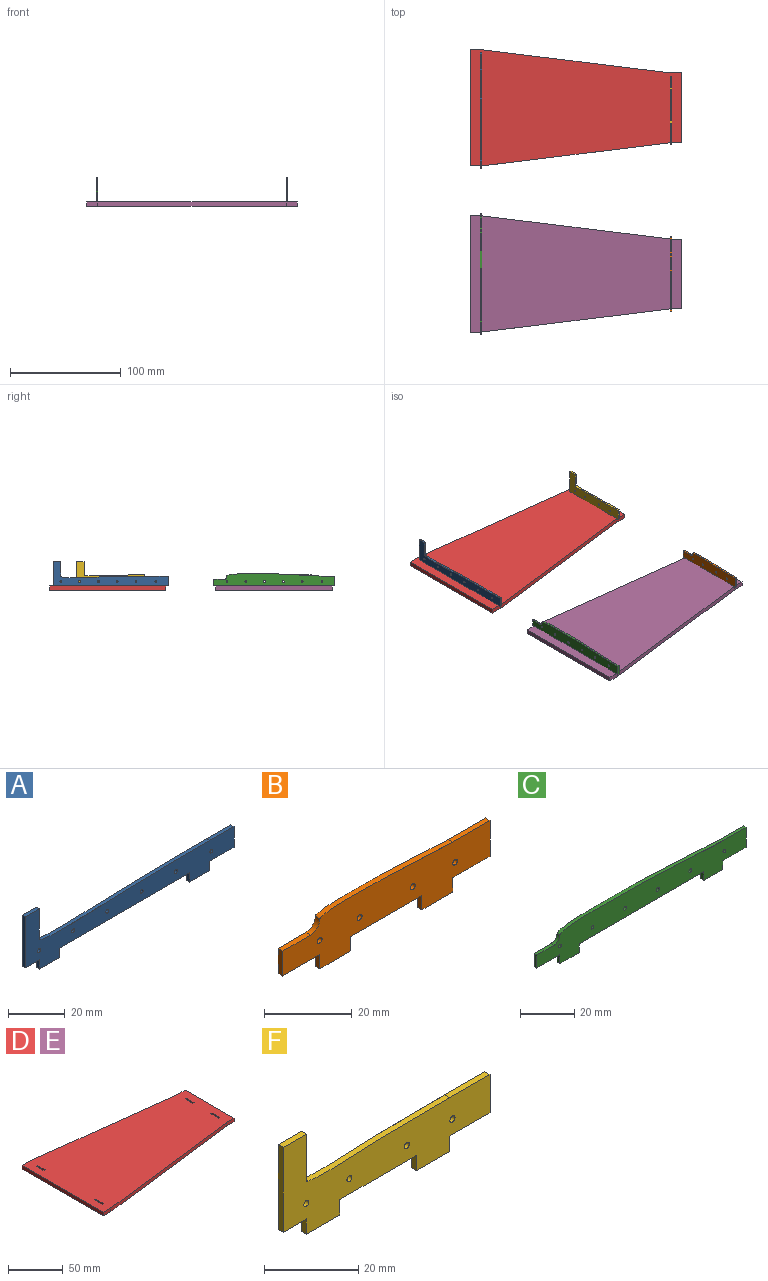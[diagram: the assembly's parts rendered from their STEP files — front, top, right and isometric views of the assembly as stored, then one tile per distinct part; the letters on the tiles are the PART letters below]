
ASSEMBLY  parts=6 mates=13
PART A: 23 faces, bbox 104x1.5x26 mm
  f0: plane 4x1.5mm, normal (1,0,0), area 6mm2, adj f1,f20,f21,f22
  f1: plane 12x1.5mm, normal (0,0,-1), area 18mm2, adj f0,f2,f21,f22
  f2: plane 8.89x1.5mm, normal (1,0,0), area 13.3mm2, adj f1,f3,f21,f22
  f3: plane 12x1.5mm, normal (0,0,1), area 18mm2, adj f2,f4,f21,f22
  f4: extruded ~85x1.61mm, area 127.8mm2, adj f3,f5,f21,f22
  f5: plane 13.08x1.5mm, normal (1,0,0), area 19.6mm2, adj f4,f6,f21,f22
  f6: plane 7x1.5mm, normal (0,0,1), area 10.5mm2, adj f5,f7,f21,f22
  f7: plane 22x1.5mm, normal (-1,0,0), area 33mm2, adj f6,f8,f21,f22
  f8: plane 7x1.5mm, normal (0,0,-1), area 10.5mm2, adj f7,f9,f21,f22
  f9: plane 4x1.5mm, normal (-1,0,0), area 6mm2, adj f8,f10,f21,f22
  f10: plane 10x1.5mm, normal (0,0,-1), area 15mm2, adj f9,f11,f21,f22
  f11: plane 4x1.5mm, normal (1,0,0), area 6mm2, adj f10,f12,f21,f22
  f12: plane 65x1.5mm, normal (0,0,-1), area 97.5mm2, adj f11,f13,f21,f22
  f13: plane 4x1.5mm, normal (-1,0,0), area 6mm2, adj f12,f20,f21,f22
  f14: cylinder r=0.76mm len=1.52mm, axis (0,1,0), area 7.2mm2, adj f21,f22
  f15: cylinder r=0.76mm len=1.52mm, axis (0,1,0), area 7.2mm2, adj f21,f22
  f16: cylinder r=0.76mm len=1.52mm, axis (0,1,0), area 7.2mm2, adj f21,f22
  f17: cylinder r=0.76mm len=1.52mm, axis (0,1,0), area 7.2mm2, adj f21,f22
  f18: cylinder r=0.76mm len=1.52mm, axis (0,1,0), area 7.2mm2, adj f21,f22
  f19: cylinder r=0.76mm len=1.52mm, axis (0,1,0), area 7.2mm2, adj f21,f22
  f20: plane 10x1.5mm, normal (0,0,-1), area 15mm2, adj f0,f13,f21,f22
  f21: plane 104x26mm, normal (0,-1,0), area 1032.6mm2, adj f0,f1,f2,f3,f4,f5,f6,f7
  f22: plane 104x26mm, normal (0,1,0), area 1032.6mm2, adj f0,f1,f2,f3,f4,f5,f6,f7
PART B: 21 faces, bbox 67x1.5x15.1 mm
  f0: plane 6.95x1.5mm, normal (-1,0,0), area 10.4mm2, adj f1,f18,f19,f20
  f1: plane 12x1.5mm, normal (0,0,-1), area 18mm2, adj f0,f2,f19,f20
  f2: plane 4x1.5mm, normal (-1,0,0), area 6mm2, adj f1,f3,f19,f20
  f3: plane 10x1.5mm, normal (0,0,-1), area 15mm2, adj f2,f4,f19,f20
  f4: plane 4x1.5mm, normal (1,0,0), area 6mm2, adj f3,f5,f19,f20
  f5: plane 23x1.5mm, normal (0,0,-1), area 34.5mm2, adj f4,f6,f19,f20
  f6: plane 4x1.5mm, normal (-1,0,0), area 6mm2, adj f5,f7,f19,f20
  f7: plane 10x1.5mm, normal (0,0,-1), area 15mm2, adj f6,f8,f19,f20
  f8: plane 4x1.5mm, normal (1,0,0), area 6mm2, adj f7,f9,f19,f20
  f9: plane 12x1.5mm, normal (0,0,-1), area 18mm2, adj f8,f10,f19,f20
  f10: plane 9.97x1.5mm, normal (1,0,0), area 14.9mm2, adj f9,f11,f19,f20
  f11: plane 12x1.5mm, normal (0,0,1), area 18mm2, adj f10,f12,f19,f20
  f12: extruded ~43x1.5mm, area 64.7mm2, adj f11,f13,f19,f20
  f13: cylinder r=3mm len=3mm, axis (0,1,0), area 7.1mm2, adj f12,f18,f19,f20
  f14: cylinder r=0.76mm len=1.52mm, axis (0,1,0), area 7.2mm2, adj f19,f20
  f15: cylinder r=0.76mm len=1.52mm, axis (0,1,0), area 7.2mm2, adj f19,f20
  f16: cylinder r=0.76mm len=1.52mm, axis (0,1,0), area 7.2mm2, adj f19,f20
  f17: cylinder r=0.76mm len=1.52mm, axis (0,1,0), area 7.2mm2, adj f19,f20
  f18: plane 9x1.5mm, normal (0,0,1), area 13.5mm2, adj f0,f13,f19,f20
  f19: plane 67x15.14mm, normal (0,-1,0), area 739.3mm2, adj f0,f1,f2,f3,f4,f5,f6,f7
  f20: plane 67x15.14mm, normal (0,1,0), area 739.3mm2, adj f0,f1,f2,f3,f4,f5,f6,f7
PART C: 23 faces, bbox 109x1.5x15.3 mm
  f0: plane 5.92x1.5mm, normal (-1,0,0), area 8.9mm2, adj f1,f20,f21,f22
  f1: plane 12x1.5mm, normal (0,0,-1), area 18mm2, adj f0,f2,f21,f22
  f2: plane 4x1.5mm, normal (-1,0,0), area 6mm2, adj f1,f3,f21,f22
  f3: plane 10x1.5mm, normal (0,0,-1), area 15mm2, adj f2,f4,f21,f22
  f4: plane 4x1.5mm, normal (1,0,0), area 6mm2, adj f3,f5,f21,f22
  f5: plane 65x1.5mm, normal (0,0,-1), area 97.5mm2, adj f4,f6,f21,f22
  f6: plane 4x1.5mm, normal (-1,0,0), area 6mm2, adj f5,f7,f21,f22
  f7: plane 10x1.5mm, normal (0,0,-1), area 15mm2, adj f6,f8,f21,f22
  f8: plane 4x1.5mm, normal (1,0,0), area 6mm2, adj f7,f9,f21,f22
  f9: plane 12x1.5mm, normal (0,0,-1), area 18mm2, adj f8,f10,f21,f22
  f10: plane 8.95x1.5mm, normal (1,0,0), area 13.4mm2, adj f9,f11,f21,f22
  f11: plane 12x1.5mm, normal (0,0,1), area 18mm2, adj f10,f12,f21,f22
  f12: extruded ~85x2.34mm, area 128.1mm2, adj f11,f13,f21,f22
  f13: cylinder r=3mm len=3mm, axis (0,1,0), area 7.1mm2, adj f12,f20,f21,f22
  f14: cylinder r=0.76mm len=1.52mm, axis (0,1,0), area 7.2mm2, adj f21,f22
  f15: cylinder r=0.76mm len=1.52mm, axis (0,1,0), area 7.2mm2, adj f21,f22
  f16: cylinder r=0.76mm len=1.52mm, axis (0,1,0), area 7.2mm2, adj f21,f22
  f17: cylinder r=0.76mm len=1.52mm, axis (0,1,0), area 7.2mm2, adj f21,f22
  f18: cylinder r=0.76mm len=1.52mm, axis (0,1,0), area 7.2mm2, adj f21,f22
  f19: cylinder r=0.76mm len=1.52mm, axis (0,1,0), area 7.2mm2, adj f21,f22
  f20: plane 9x1.5mm, normal (0,0,1), area 13.5mm2, adj f0,f13,f21,f22
  f21: plane 109x15.27mm, normal (0,-1,0), area 1139.9mm2, adj f0,f1,f2,f3,f4,f5,f6,f7
  f22: plane 109x15.27mm, normal (0,1,0), area 1139.9mm2, adj f0,f1,f2,f3,f4,f5,f6,f7
PART D: 26 faces, bbox 190x105x4 mm
  f0: plane 4x1.5mm, normal (0,-1,0), area 6mm2, adj f1,f23,f24,f25
  f1: plane 10x4mm, normal (-1,0,0), area 40mm2, adj f0,f2,f24,f25
  f2: plane 4x1.5mm, normal (0,1,0), area 6mm2, adj f1,f23,f24,f25
  f3: plane 4x1.5mm, normal (0,1,0), area 6mm2, adj f4,f19,f24,f25
  f4: plane 10x4mm, normal (1,0,0), area 40mm2, adj f3,f5,f24,f25
  f5: plane 4x1.5mm, normal (0,-1,0), area 6mm2, adj f4,f19,f24,f25
  f6: plane 10x4mm, normal (1,0,0), area 40mm2, adj f7,f20,f24,f25
  f7: plane 4x1.5mm, normal (0,-1,0), area 6mm2, adj f6,f8,f24,f25
  f8: plane 10x4mm, normal (-1,0,0), area 40mm2, adj f7,f20,f24,f25
  f9: plane 10x4mm, normal (-1,0,0), area 40mm2, adj f10,f21,f24,f25
  f10: plane 4x1.5mm, normal (0,1,0), area 6mm2, adj f9,f11,f24,f25
  f11: plane 10x4mm, normal (1,0,0), area 40mm2, adj f10,f21,f24,f25
  f12: plane 10x4mm, normal (0,1,0), area 40mm2, adj f13,f22,f24,f25
  f13: plane 170x21mm, normal (0.12,0.99,0), area 685.2mm2, adj f12,f14,f24,f25
  f14: plane 10x4mm, normal (0,1,0), area 40mm2, adj f13,f15,f24,f25
  f15: plane 105x4mm, normal (-1,0,0), area 420mm2, adj f14,f16,f24,f25
  f16: plane 10x4mm, normal (0,-1,0), area 40mm2, adj f15,f17,f24,f25
  f17: plane 170x21mm, normal (0.12,-0.99,0), area 685.2mm2, adj f16,f18,f24,f25
  f18: plane 10x4mm, normal (0,-1,0), area 40mm2, adj f17,f22,f24,f25
  f19: plane 10x4mm, normal (-1,0,0), area 40mm2, adj f3,f5,f24,f25
  f20: plane 4x1.5mm, normal (0,1,0), area 6mm2, adj f6,f8,f24,f25
  f21: plane 4x1.5mm, normal (0,-1,0), area 6mm2, adj f9,f11,f24,f25
  f22: plane 63x4mm, normal (1,0,0), area 252mm2, adj f12,f18,f24,f25
  f23: plane 10x4mm, normal (1,0,0), area 40mm2, adj f0,f2,f24,f25
  f24: plane 190x105mm, normal (0,0,1), area 15900mm2, adj f0,f1,f2,f3,f4,f5,f6,f7
  f25: plane 190x105mm, normal (0,0,-1), area 15900mm2, adj f0,f1,f2,f3,f4,f5,f6,f7
PART E: same geometry as D
PART F: 21 faces, bbox 62x1.5x26 mm
  f0: plane 12x1.5mm, normal (0,0,1), area 18mm2, adj f1,f17,f19,f20
  f1: extruded ~43x1.5mm, area 64.7mm2, adj f0,f2,f19,f20
  f2: plane 12.05x1.5mm, normal (1,0,0), area 18.1mm2, adj f1,f3,f19,f20
  f3: plane 7x1.5mm, normal (0,0,1), area 10.5mm2, adj f2,f4,f19,f20
  f4: plane 22x1.5mm, normal (-1,0,0), area 33mm2, adj f3,f5,f19,f20
  f5: plane 7x1.5mm, normal (0,0,-1), area 10.5mm2, adj f4,f6,f19,f20
  f6: plane 4x1.5mm, normal (-1,0,0), area 6mm2, adj f5,f7,f19,f20
  f7: plane 10x1.5mm, normal (0,0,-1), area 15mm2, adj f6,f8,f19,f20
  f8: plane 4x1.5mm, normal (1,0,0), area 6mm2, adj f7,f9,f19,f20
  f9: plane 23x1.5mm, normal (0,0,-1), area 34.5mm2, adj f8,f10,f19,f20
  f10: plane 4x1.5mm, normal (-1,0,0), area 6mm2, adj f9,f11,f19,f20
  f11: plane 10x1.5mm, normal (0,0,-1), area 15mm2, adj f10,f12,f19,f20
  f12: plane 4x1.5mm, normal (1,0,0), area 6mm2, adj f11,f13,f19,f20
  f13: plane 12x1.5mm, normal (0,0,-1), area 18mm2, adj f12,f17,f19,f20
  f14: cylinder r=0.76mm len=1.52mm, axis (0,1,0), area 7.2mm2, adj f19,f20
  f15: cylinder r=0.76mm len=1.52mm, axis (0,1,0), area 7.2mm2, adj f19,f20
  f16: cylinder r=0.76mm len=1.52mm, axis (0,1,0), area 7.2mm2, adj f19,f20
  f17: plane 9.93x1.5mm, normal (1,0,0), area 14.9mm2, adj f0,f13,f19,f20
  f18: cylinder r=0.76mm len=1.52mm, axis (0,1,0), area 7.2mm2, adj f19,f20
  f19: plane 62x26mm, normal (0,-1,0), area 759.6mm2, adj f0,f1,f2,f3,f4,f5,f6,f7
  f20: plane 62x26mm, normal (0,1,0), area 759.6mm2, adj f0,f1,f2,f3,f4,f5,f6,f7
PLACE A rot(axis=(0,0,-1),90deg) t=(-68.05,-5.62,67.36)mm
PLACE B rot(axis=(0,0,-1),90deg) t=(103.45,129.09,83.9)mm
PLACE C rot(axis=(0,0,-1),90deg) t=(-68.05,-152.07,121.77)mm
PLACE D t=(0,150,0)mm
PLACE E at identity fixed
PLACE F rot(axis=(0,0,-1),90deg) t=(103.45,278.05,48.38)mm
MATE planar E.f5 <-> B.f6  axis (0,-1,0) through (102.7,-13.55,2)mm
MATE planar D.f10 <-> A.f0  axis (0,1,0) through (-68.8,105.45,2)mm
MATE planar E.f4 <-> B.f19  axis (1,0,0) through (101.95,-18.55,2)mm
MATE planar E.f9 <-> C.f22  axis (-1,0,0) through (-68.05,-39.55,2)mm
MATE planar C.f6 <-> E.f21  axis (0,1,0) through (-68.8,-34.55,2)mm
MATE planar E.f25 <-> D.f25  axis (0,0,-1) through (8.21,-2.05,0)mm
MATE planar E.f24 <-> B.f5  axis (0,0,1) through (8.21,-2.05,4)mm
MATE planar D.f3 <-> F.f12  axis (0,1,0) through (102.7,126.45,2)mm
MATE planar D.f24 <-> A.f12  axis (0,0,1) through (8.21,147.95,4)mm
MATE planar D.f4 <-> F.f19  axis (1,0,0) through (101.95,131.45,2)mm
MATE planar E.f24 <-> C.f5  axis (0,0,1) through (8.21,-2.05,4)mm
MATE planar D.f9 <-> A.f22  axis (-1,0,0) through (-68.05,110.45,2)mm
MATE planar D.f24 <-> F.f9  axis (0,0,1) through (8.21,147.95,4)mm
